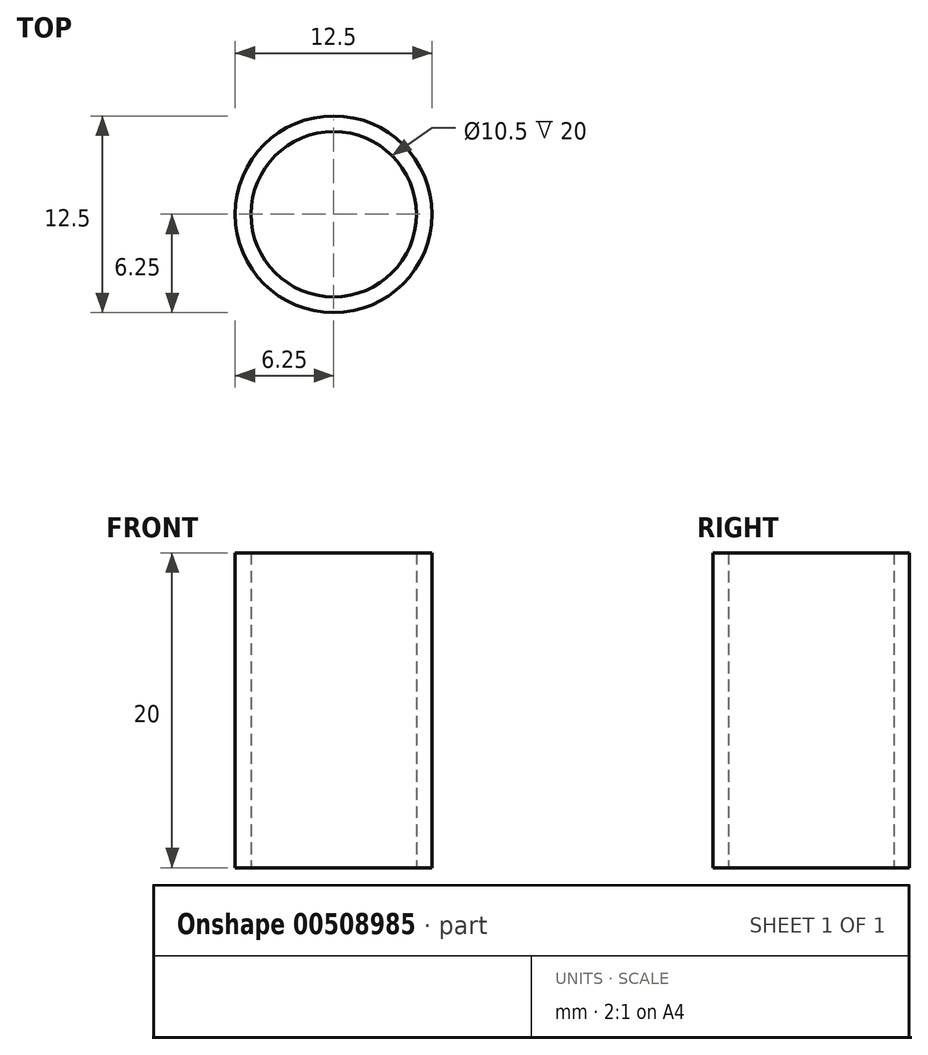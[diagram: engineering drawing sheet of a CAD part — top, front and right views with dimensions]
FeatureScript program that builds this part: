
annotation { "Feature Type Name" : "Feature", "Feature Type Description" : "" }
export const myFeature = defineFeature(function(context is Context, id is Id, definition is map)
    precondition{}
    {
        {
            var Q0;
            Q0=qCreatedBy(makeId("Top.planeOp"),FACE);
            var sketch = newSketch(context, id + "F0", { "sketchPlane" : qUnion([Q0])});
            skCircle(sketch, "E0", {"center": v(0, 0) * mm, "radius": 6.25 * mm});
            skCircle(sketch, "E1", {"center": v(0, 0) * mm, "radius": 5.25 * mm});
            skSolve(sketch);
        }
        {
            var Q0;
            Q0=makeQuery(id+"F0.imprint","IMPRINT",FACE,{"disambiguationData":[TD([[makeQuery(id+"F0.imprint","IMPRINT",EDGE,{"derivedFrom":sQuery(id+"F0.wireOp",EDGE,"E0")}),1.0]])]});
            extrude(context, id + "F1", {"entities" : qUnion([Q0]), "depth" : 20 * mm});
        }
    });
